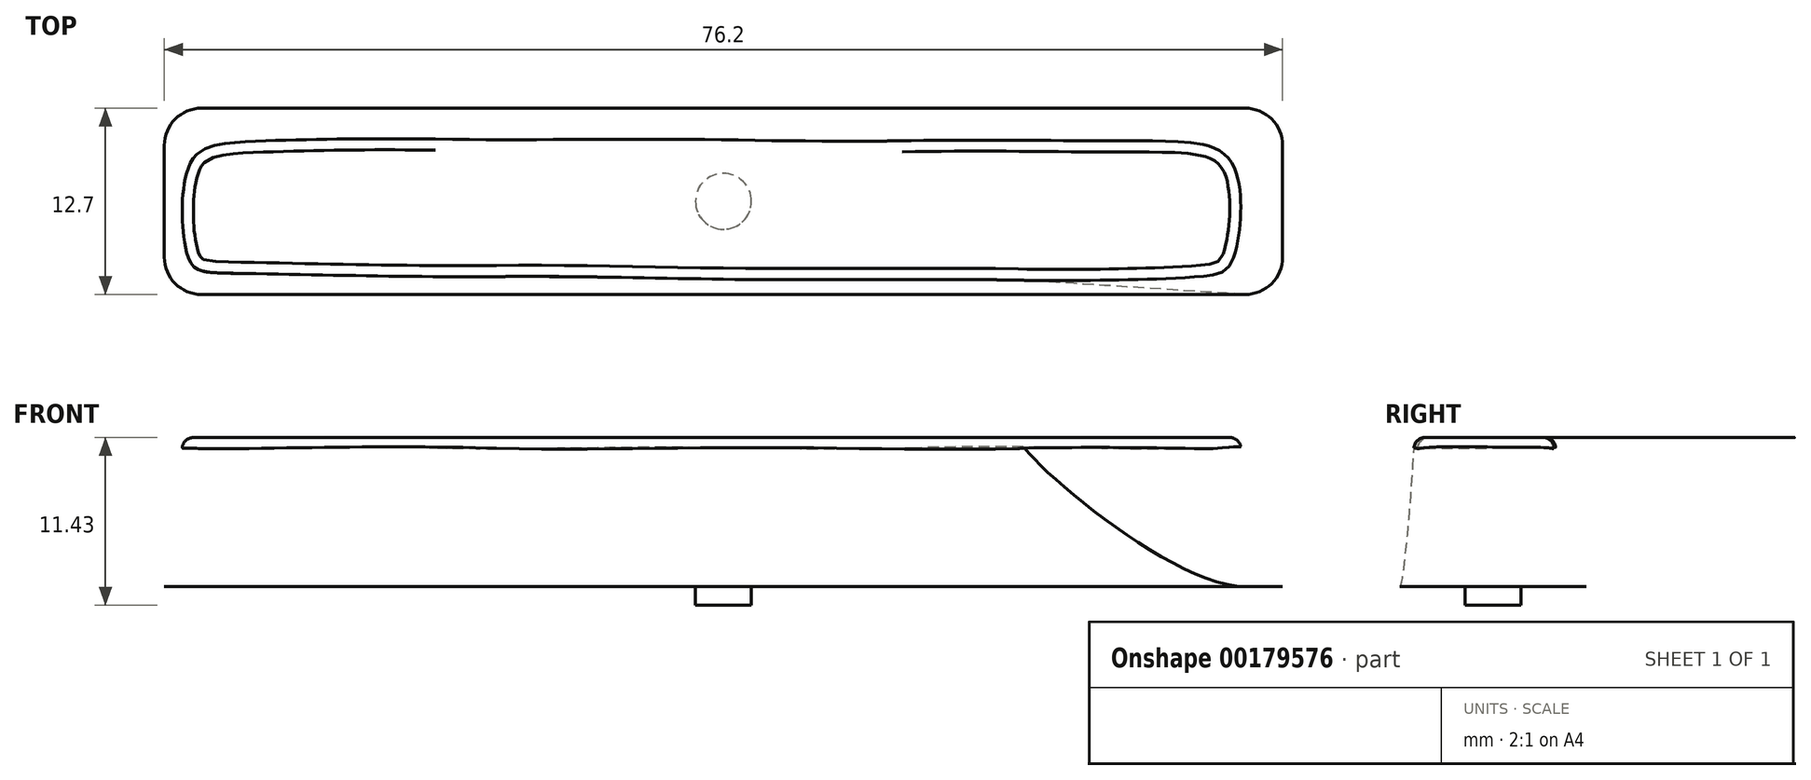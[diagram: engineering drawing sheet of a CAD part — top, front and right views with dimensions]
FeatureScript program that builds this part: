
annotation { "Feature Type Name" : "Feature", "Feature Type Description" : "" }
export const myFeature = defineFeature(function(context is Context, id is Id, definition is map)
    precondition{}
    {
        {
            var Q0;
            Q0=qCreatedBy(makeId("Top.planeOp"),FACE);
            var sketch = newSketch(context, id + "F0", { "sketchPlane" : qUnion([Q0])});
            skLineSegment(sketch, "E0.bottom", {"start": v(2.54, 0) * mm, "end": v(73.66, 0) * mm});
            skLineSegment(sketch, "E0.top", {"start": v(2.54, 12.7) * mm, "end": v(73.66, 12.7) * mm});
            skLineSegment(sketch, "E0.left", {"start": v(0, 2.54) * mm, "end": v(0, 10.16) * mm});
            skLineSegment(sketch, "E0.right", {"start": v(76.2, 2.54) * mm, "end": v(76.2, 10.16) * mm});
            skPoint(sketch, "E1.visualSharp", {"position": v(0, 12.7) * mm});
            skArc(sketch, "E1.filletArc", {"start": v(2.54, 12.7) * mm, "mid": v(0.74, 11.96) * mm, "end": v(0, 10.16) * mm});
            skPoint(sketch, "E2.visualSharp", {"position": v(76.2, 12.7) * mm});
            skArc(sketch, "E2.filletArc", {"start": v(76.2, 10.16) * mm, "mid": v(75.46, 11.96) * mm, "end": v(73.66, 12.7) * mm});
            skPoint(sketch, "E3.visualSharp", {"position": v(76.2, 0) * mm});
            skArc(sketch, "E3.filletArc", {"start": v(73.66, 0) * mm, "mid": v(75.46, 0.74) * mm, "end": v(76.2, 2.54) * mm});
            skPoint(sketch, "E4.visualSharp", {"position": v(0, 0) * mm});
            skArc(sketch, "E4.filletArc", {"start": v(0, 2.54) * mm, "mid": v(0.74, 0.74) * mm, "end": v(2.54, 0) * mm});
            skSolve(sketch);
        }
        {
            var Q0;
            Q0=qCreatedBy(makeId("Top.planeOp"),FACE);
            cPlane(context, id + "F1", {"entities" : qUnion([Q0]), "cplaneType" : CPlaneType.OFFSET, "offset" : 10.16 * mm, "width" : 152.4 * mm, "height" : 152.4 * mm});
        }
        {
            var Q0;
            Q0=qCreatedBy(id+"F1.planeOp",FACE);
            var sketch = newSketch(context, id + "F2", { "sketchPlane" : qUnion([Q0])});
            skFitSpline(sketch, "E5", {"points": [v(1.7, 8.66) * mm, v(7.03, 10.44) * mm, v(64.12, 10.44) * mm, v(72.83, 8.66) * mm, v(72.78, 2.54) * mm, v(69.55, 1.16) * mm, v(5.42, 1.43) * mm, v(1.66, 2.54) * mm, v(1.7, 8.66) * mm]});
            skLineSegment(sketch, "E6", {"start": v(1.66, 2.54) * mm, "end": v(72.78, 2.54) * mm, "construction": true});
            skLineSegment(sketch, "E7", {"start": v(1.7, 8.66) * mm, "end": v(72.83, 8.66) * mm, "construction": true});
            skSolve(sketch);
        }
        {
            var Q0;
            Q0=qCreatedBy(id+"F1.planeOp",FACE);
            cPlane(context, id + "F3", {"entities" : qUnion([Q0]), "cplaneType" : CPlaneType.OFFSET, "offset" : 1.27 * mm, "oppositeDirection" : true, "width" : 152.4 * mm, "height" : 152.4 * mm});
        }
        {
            var Q0;
            Q0=makeQuery(id+"F0.imprint","IMPRINT",FACE,{"disambiguationData":[TD([[makeQuery(id+"F0.imprint","IMPRINT",EDGE,{"derivedFrom":sQuery(id+"F0.wireOp",EDGE,"E0.bottom")}),1.0]])]});
            var Q1;
            Q1=makeQuery(id+"F2.imprint","IMPRINT",FACE,{"disambiguationData":[TD([[makeQuery(id+"F2.imprint","IMPRINT",EDGE,{"derivedFrom":sQuery(id+"F2.wireOp",EDGE,"E5")}),-1.0]])]});
            var Q2;
            Q2=sQuery(id+"F2.wireOp",VERTEX,"E6.end");
            var Q3;
            Q3=sQuery(id+"F0.wireOp",VERTEX,"E0.right.start");
            loft(context, id + "F4", {"startCondition" : LoftEndDerivativeType.TANGENT_TO_PROFILE, "startMagnitude" : 1, "endCondition" : LoftEndDerivativeType.NORMAL_TO_PROFILE, "endMagnitude" : 0.3, "sheetProfilesArray" : [{ "sheetProfileEntities" : qUnion([Q0]) }, { "sheetProfileEntities" : qUnion([Q1]) }], "matchConnections" : true, "connections" : [{ "connectionEntities" : qUnion([Q2, Q3]), "connectionEdgeQueries" : qUnion([]), "connectionEdgeParameters" : [] }]});
        }
        {
            var Q0;
            {var subQ0=sQuery(id+"F2.wireOp",EDGE,"E5");var subQ1=sQuery(id+"F0.wireOp",EDGE,"E4.filletArc");var subQ2=sQuery(id+"F0.wireOp",EDGE,"E3.filletArc");var subQ3=sQuery(id+"F0.wireOp",EDGE,"E0.bottom");Q0=makeQuery(id+"F9a73gEcRfjhf6K_1.boolean.opBoolean","MERGE",EDGE,{"derivedFrom":[makeQuery(id+"F4.opLoft","MID_CAP_EDGE",EDGE,{"disambiguationData":[OSD([subQ3,subQ2,subQ1,subQ0])],"capPos":1.0}),makeQuery(id+"F9a73gEcRfjhf6K_1.opLoft","MID_CAP_EDGE",EDGE,{"disambiguationData":[OSD([subQ3,subQ2,subQ1,subQ0])],"capPos":0.0})]});}
            var Q1;
            {var subQ0=sQuery(id+"F2.wireOp",EDGE,"E5");var subQ1=sQuery(id+"F0.wireOp",EDGE,"E3.filletArc");var subQ2=sQuery(id+"F0.wireOp",EDGE,"E0.right");var subQ3=sQuery(id+"F0.wireOp",EDGE,"E0.bottom");Q1=makeQuery(id+"F9a73gEcRfjhf6K_1.boolean.opBoolean","MERGE",EDGE,{"derivedFrom":[makeQuery(id+"F4.opLoft","MID_CAP_EDGE",EDGE,{"disambiguationData":[OSD([subQ3,subQ2,subQ1,subQ0])],"capPos":1.0}),makeQuery(id+"F9a73gEcRfjhf6K_1.opLoft","MID_CAP_EDGE",EDGE,{"disambiguationData":[OSD([subQ3,subQ2,subQ1,subQ0])],"capPos":0.0})]});}
            var Q2;
            {var subQ0=sQuery(id+"F2.wireOp",EDGE,"E5");var subQ1=sQuery(id+"F0.wireOp",EDGE,"E3.filletArc");var subQ2=sQuery(id+"F0.wireOp",EDGE,"E2.filletArc");var subQ3=sQuery(id+"F0.wireOp",EDGE,"E0.right");Q2=makeQuery(id+"F9a73gEcRfjhf6K_1.boolean.opBoolean","MERGE",EDGE,{"derivedFrom":[makeQuery(id+"F4.opLoft","MID_CAP_EDGE",EDGE,{"disambiguationData":[OSD([subQ3,subQ2,subQ1,subQ0])],"capPos":1.0}),makeQuery(id+"F9a73gEcRfjhf6K_1.opLoft","MID_CAP_EDGE",EDGE,{"disambiguationData":[OSD([subQ3,subQ2,subQ1,subQ0])],"capPos":0.0})]});}
            var Q3;
            {var subQ0=sQuery(id+"F2.wireOp",EDGE,"E5");var subQ1=sQuery(id+"F0.wireOp",EDGE,"E2.filletArc");var subQ2=sQuery(id+"F0.wireOp",EDGE,"E0.right");var subQ3=sQuery(id+"F0.wireOp",EDGE,"E0.top");Q3=makeQuery(id+"F9a73gEcRfjhf6K_1.boolean.opBoolean","MERGE",EDGE,{"derivedFrom":[makeQuery(id+"F4.opLoft","MID_CAP_EDGE",EDGE,{"disambiguationData":[OSD([subQ3,subQ2,subQ1,subQ0])],"capPos":1.0}),makeQuery(id+"F9a73gEcRfjhf6K_1.opLoft","MID_CAP_EDGE",EDGE,{"disambiguationData":[OSD([subQ3,subQ2,subQ1,subQ0])],"capPos":0.0})]});}
            var Q4;
            {var subQ0=sQuery(id+"F2.wireOp",EDGE,"E5");var subQ1=sQuery(id+"F0.wireOp",EDGE,"E2.filletArc");var subQ2=sQuery(id+"F0.wireOp",EDGE,"E1.filletArc");var subQ3=sQuery(id+"F0.wireOp",EDGE,"E0.top");Q4=makeQuery(id+"F9a73gEcRfjhf6K_1.boolean.opBoolean","MERGE",EDGE,{"derivedFrom":[makeQuery(id+"F4.opLoft","MID_CAP_EDGE",EDGE,{"disambiguationData":[OSD([subQ3,subQ2,subQ1,subQ0])],"capPos":1.0}),makeQuery(id+"F9a73gEcRfjhf6K_1.opLoft","MID_CAP_EDGE",EDGE,{"disambiguationData":[OSD([subQ3,subQ2,subQ1,subQ0])],"capPos":0.0})]});}
            var Q5;
            {var subQ0=sQuery(id+"F2.wireOp",EDGE,"E5");var subQ1=sQuery(id+"F0.wireOp",EDGE,"E1.filletArc");var subQ2=sQuery(id+"F0.wireOp",EDGE,"E0.left");var subQ3=sQuery(id+"F0.wireOp",EDGE,"E0.top");Q5=makeQuery(id+"F9a73gEcRfjhf6K_1.boolean.opBoolean","MERGE",EDGE,{"derivedFrom":[makeQuery(id+"F4.opLoft","MID_CAP_EDGE",EDGE,{"disambiguationData":[OSD([subQ3,subQ2,subQ1,subQ0])],"capPos":1.0}),makeQuery(id+"F9a73gEcRfjhf6K_1.opLoft","MID_CAP_EDGE",EDGE,{"disambiguationData":[OSD([subQ3,subQ2,subQ1,subQ0])],"capPos":0.0})]});}
            var Q6;
            {var subQ0=sQuery(id+"F2.wireOp",EDGE,"E5");var subQ1=sQuery(id+"F0.wireOp",EDGE,"E4.filletArc");var subQ2=sQuery(id+"F0.wireOp",EDGE,"E1.filletArc");var subQ3=sQuery(id+"F0.wireOp",EDGE,"E0.left");var subQ4=sQuery(id+"F0.wireOp",EDGE,"E0.bottom");Q6=makeQuery(id+"F9a73gEcRfjhf6K_1.boolean.opBoolean","MERGE",EDGE,{"derivedFrom":[makeQuery(id+"F4.opLoft","MID_CAP_EDGE",EDGE,{"disambiguationData":[OSD([subQ4,subQ3,subQ2,subQ1,subQ0])],"capPos":1.0}),makeQuery(id+"F9a73gEcRfjhf6K_1.opLoft","MID_CAP_EDGE",EDGE,{"disambiguationData":[OSD([subQ4,subQ3,subQ2,subQ1,subQ0])],"capPos":0.0})]});}
            var Q7;
            {var subQ0=sQuery(id+"F2.wireOp",EDGE,"E5");var subQ1=sQuery(id+"F0.wireOp",EDGE,"E4.filletArc");var subQ2=sQuery(id+"F0.wireOp",EDGE,"E0.bottom");Q7=makeQuery(id+"F9a73gEcRfjhf6K_1.boolean.opBoolean","MERGE",EDGE,{"derivedFrom":[makeQuery(id+"F4.opLoft","MID_CAP_EDGE",EDGE,{"disambiguationData":[OSD([subQ2,subQ1,subQ0])],"capPos":1.0}),makeQuery(id+"F9a73gEcRfjhf6K_1.opLoft","MID_CAP_EDGE",EDGE,{"disambiguationData":[OSD([subQ2,subQ1,subQ0])],"capPos":0.0})]});}
            fillet(context, id + "F5", {"entities" : qUnion([Q0, Q1, Q2, Q3, Q4, Q5, Q6, Q7]), "radius" : 0.76 * mm, "tangentPropagation" : true, "allowEdgeOverflow" : false});
        }
        {
            var Q0;
            Q0=makeQuery(id+"F4.opLoft","CAP_FACE",FACE,{"disambiguationData":[OSD([makeQuery(id+"F0.imprint","IMPRINT",FACE,{"disambiguationData":[TD([[makeQuery(id+"F0.imprint","IMPRINT",EDGE,{"derivedFrom":sQuery(id+"F0.wireOp",EDGE,"E0.bottom")}),1.0]])]})])],"isStart":true});
            var sketch = newSketch(context, id + "F6", { "sketchPlane" : qUnion([Q0])});
            skPoint(sketch, "E8", {"position": v(38.1, -6.35) * mm});
            skPoint(sketch, "E9.0", {"position": v(38.1, 0) * mm});
            skPoint(sketch, "E10.0", {"position": v(76.2, -6.35) * mm});
            skCircle(sketch, "E11", {"center": v(38.1, -6.35) * mm, "radius": 1.9 * mm});
            skSolve(sketch);
        }
        {
            var Q0;
            Q0=qSketchRegion(id+"F6",true);
            extrude(context, id + "F7", {"entities" : qUnion([Q0]), "operationType" : NewBodyOperationType.ADD, "depth" : 1.27 * mm});
        }
    });
